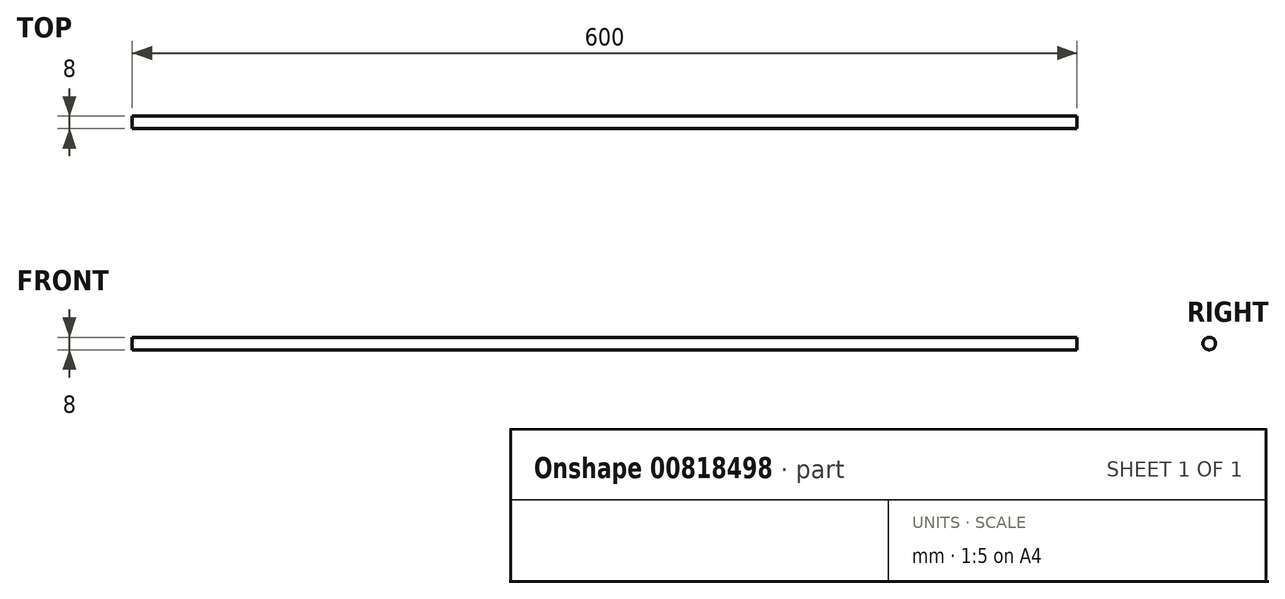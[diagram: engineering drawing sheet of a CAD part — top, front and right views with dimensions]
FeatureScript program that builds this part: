
annotation { "Feature Type Name" : "Feature", "Feature Type Description" : "" }
export const myFeature = defineFeature(function(context is Context, id is Id, definition is map)
    precondition{}
    {
        {
            var Q0;
            Q0=qCreatedBy(makeId("Right.planeOp"),FACE);
            var sketch = newSketch(context, id + "F0", { "sketchPlane" : qUnion([Q0])});
            skCircle(sketch, "E0", {"center": v(0, 0) * mm, "radius": 4 * mm});
            skSolve(sketch);
        }
        {
            var Q0;
            Q0=qSketchRegion(id+"F0",true);
            extrude(context, id + "F1", {"entities" : qUnion([Q0]), "endBound" : BoundingType.SYMMETRIC, "depth" : 600 * mm});
        }
    });
